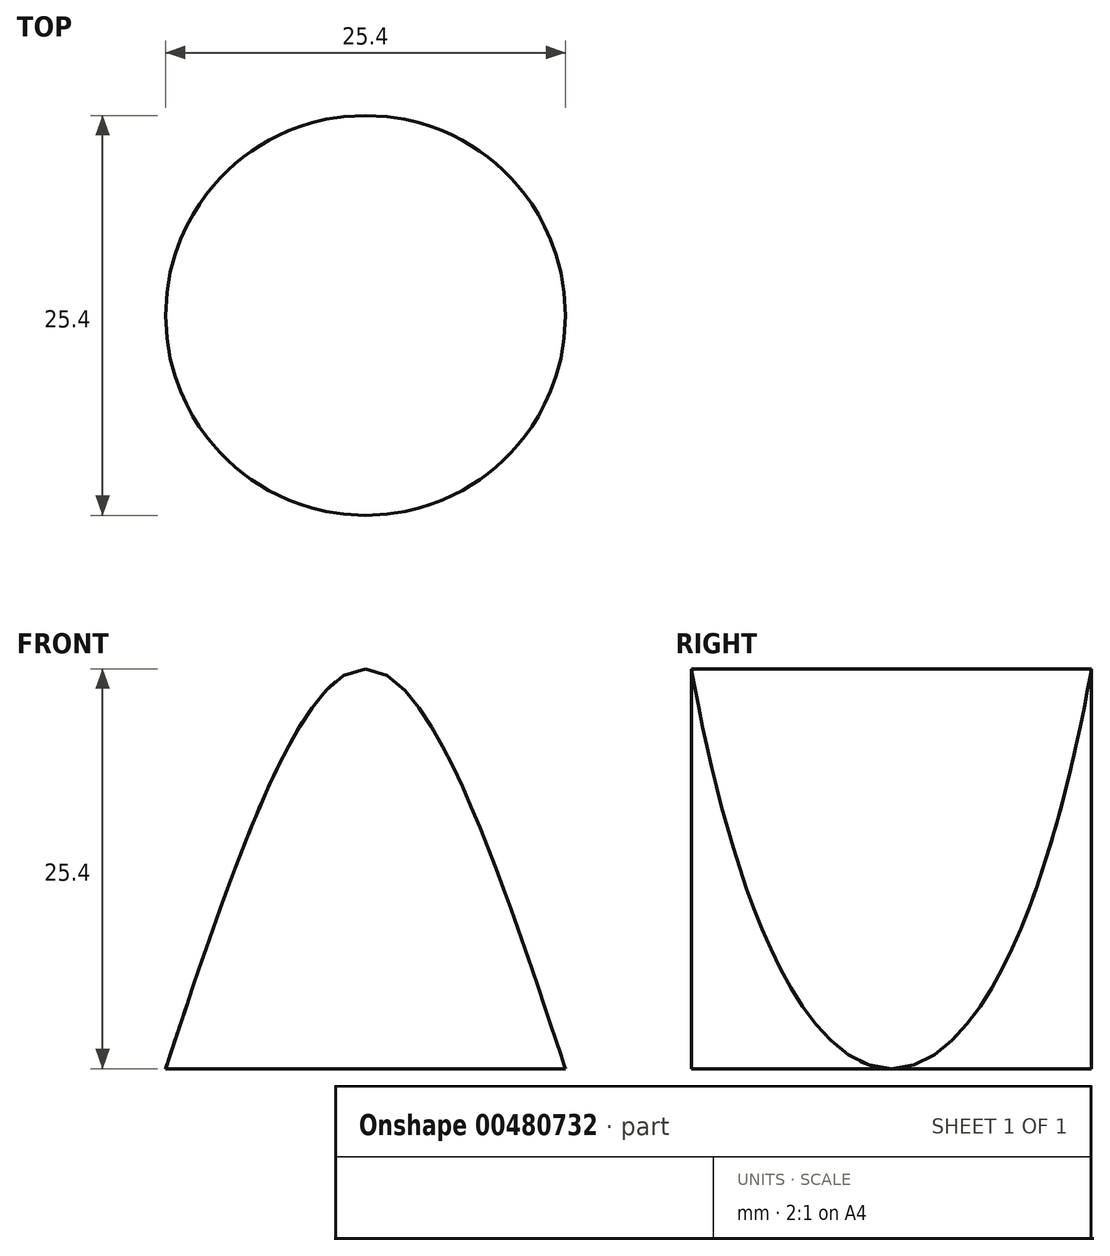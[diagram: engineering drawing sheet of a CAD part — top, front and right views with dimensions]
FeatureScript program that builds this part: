
annotation { "Feature Type Name" : "Feature", "Feature Type Description" : "" }
export const myFeature = defineFeature(function(context is Context, id is Id, definition is map)
    precondition{}
    {
        {
            var Q0;
            Q0=qCreatedBy(makeId("Top.planeOp"),FACE);
            var sketch = newSketch(context, id + "F0", { "sketchPlane" : qUnion([Q0])});
            skCircle(sketch, "E0", {"center": v(0, 0) * mm, "radius": 12.7 * mm});
            skSolve(sketch);
        }
        {
            var Q0;
            Q0=makeQuery(id+"F0.imprint","IMPRINT",FACE,{"disambiguationData":[TD([[makeQuery(id+"F0.imprint","IMPRINT",EDGE,{"derivedFrom":sQuery(id+"F0.wireOp",EDGE,"E0")}),1.0]])]});
            extrude(context, id + "F1", {"entities" : qUnion([Q0]), "depth" : 25.4 * mm});
        }
        {
            var Q0;
            Q0=qCreatedBy(makeId("Front.planeOp"),FACE);
            var sketch = newSketch(context, id + "F2", { "sketchPlane" : qUnion([Q0])});
            skLineSegment(sketch, "E1", {"start": v(-12.7, 0) * mm, "end": v(-12.7, 25.4) * mm});
            skLineSegment(sketch, "E2", {"start": v(12.7, 25.4) * mm, "end": v(12.7, 0) * mm});
            skLineSegment(sketch, "E3.0", {"start": v(-12.7, 25.4) * mm, "end": v(12.7, 25.4) * mm});
            skFitSpline(sketch, "E4", {"points": [v(-12.7, 0) * mm, v(0, 25.4) * mm, v(12.7, 0) * mm], "startDerivative": vector(25.4, 76.2) * mm, "endDerivative": vector(25.4, -76.2) * mm});
            skSolve(sketch);
        }
        {
            var Q0;
            {var subQ0=sQuery(id+"F2.wireOp",EDGE,"E1");Q0=makeQuery(id+"F2.imprint","IMPRINT",FACE,{"disambiguationData":[TD([[makeQuery(id+"F2.imprint","IMPRINT",EDGE,{"derivedFrom":subQ0}),-1.0]])]});}
            var Q1;
            {var subQ0=sQuery(id+"F2.wireOp",EDGE,"E2");Q1=makeQuery(id+"F2.imprint","IMPRINT",FACE,{"disambiguationData":[TD([[makeQuery(id+"F2.imprint","IMPRINT",EDGE,{"derivedFrom":subQ0}),-1.0]])]});}
            extrude(context, id + "F3", {"entities" : qUnion([Q0, Q1]), "operationType" : NewBodyOperationType.REMOVE, "endBound" : BoundingType.SYMMETRIC, "depth" : 50.8 * mm});
        }
        {
            var Q0;
            Q0=qCreatedBy(makeId("Front.planeOp"),FACE);
            cPlane(context, id + "F4", {"entities" : qUnion([Q0]), "cplaneType" : CPlaneType.OFFSET, "offset" : 25.4 * mm, "width" : 152.4 * mm, "height" : 152.4 * mm});
        }
        {
            var Q0;
            Q0=qCreatedBy(id+"F4.planeOp",FACE);
            var sketch = newSketch(context, id + "F5", { "sketchPlane" : qUnion([Q0])});
            skLineSegment(sketch, "E5", {"start": v(-12.7, 0) * mm, "end": v(-12.7, 25.4) * mm});
            skLineSegment(sketch, "E6.0", {"start": v(-12.7, 25.4) * mm, "end": v(12.7, 25.4) * mm});
            skLineSegment(sketch, "E7", {"start": v(12.7, 25.4) * mm, "end": v(12.7, 0) * mm});
            skLineSegment(sketch, "E8.0", {"start": v(-12.7, 0) * mm, "end": v(12.7, 0) * mm});
            skFitSpline(sketch, "E9", {"points": [v(-12.7, 0) * mm, v(0, 25.4) * mm, v(12.7, 0) * mm], "startDerivative": vector(25.4, 76.2) * mm, "endDerivative": vector(25.4, -76.2) * mm});
            skLineSegment(sketch, "E10", {"start": v(0, 25.4) * mm, "end": v(-12.7, 25.4) * mm});
            skLineSegment(sketch, "E11", {"start": v(12.7, 0) * mm, "end": v(12.7, 25.4) * mm});
            skLineSegment(sketch, "E12", {"start": v(0, 25.4) * mm, "end": v(12.7, 25.4) * mm});
            skSolve(sketch);
        }
        {
            var Q0;
            {var subQ0=sQuery(id+"F5.wireOp",EDGE,"E11");Q0=makeQuery(id+"F5.imprint","IMPRINT",FACE,{"disambiguationData":[TD([[makeQuery(id+"F5.imprint","IMPRINT",EDGE,{"derivedFrom":subQ0}),1.0]])]});}
            var Q1;
            {var subQ0=sQuery(id+"F5.wireOp",EDGE,"E5");Q1=makeQuery(id+"F5.imprint","IMPRINT",FACE,{"disambiguationData":[TD([[makeQuery(id+"F5.imprint","IMPRINT",EDGE,{"derivedFrom":subQ0}),-1.0]])]});}
            extrude(context, id + "F6", {"entities" : qUnion([Q0, Q1]), "operationType" : NewBodyOperationType.REMOVE, "oppositeDirection" : true, "depth" : 76.2 * mm});
        }
    });
